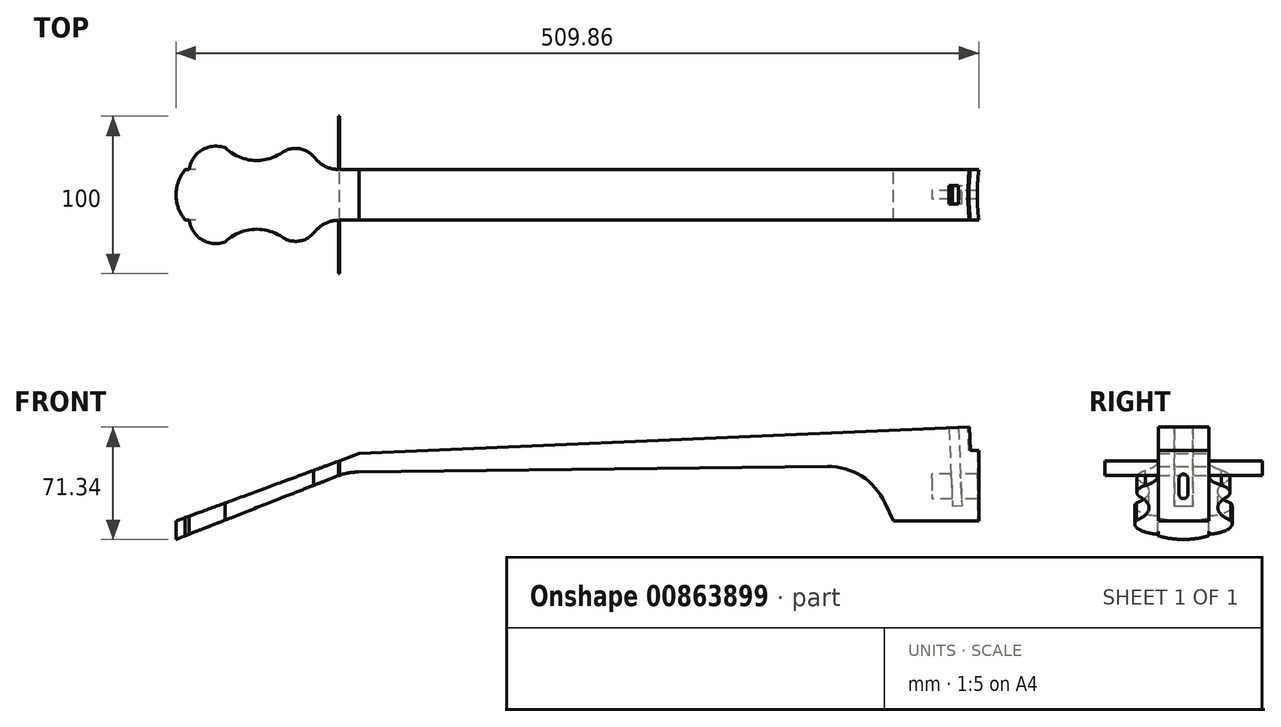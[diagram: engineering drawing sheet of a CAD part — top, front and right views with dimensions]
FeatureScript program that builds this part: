
annotation { "Feature Type Name" : "Feature", "Feature Type Description" : "" }
export const myFeature = defineFeature(function(context is Context, id is Id, definition is map)
    precondition{}
    {
        {
            var Q0;
            Q0=qCreatedBy(makeId("Front.planeOp"),FACE);
            var sketch = newSketch(context, id + "F0", { "sketchPlane" : qUnion([Q0])});
            skLineSegment(sketch, "E0.bottom", {"start": v(-76.22, 15.21) * mm, "end": v(250.9, 15.21) * mm});
            skLineSegment(sketch, "E0.top", {"start": v(195.63, -44.79) * mm, "end": v(250.9, -44.79) * mm});
            skLineSegment(sketch, "E0.right", {"start": v(250.9, 15.21) * mm, "end": v(250.9, -44.79) * mm});
            skPoint(sketch, "E1.orphan", {"position": v(250.9, 0) * mm});
            skLineSegment(sketch, "E2.bottom", {"start": v(250.9, 15.21) * mm, "end": v(-260.04, 15.21) * mm, "construction": true});
            skLineSegment(sketch, "E2.top", {"start": v(250.9, -44.79) * mm, "end": v(-260.04, -44.79) * mm, "construction": true});
            skLineSegment(sketch, "E2.left", {"start": v(250.9, 15.21) * mm, "end": v(250.9, -44.79) * mm, "construction": true});
            skLineSegment(sketch, "E2.right", {"start": v(-260.04, 15.21) * mm, "end": v(-260.04, -44.79) * mm, "construction": true});
            skLineSegment(sketch, "E3", {"start": v(250.9, 15.21) * mm, "end": v(-143.72, -2.02) * mm});
            skLineSegment(sketch, "E4", {"start": v(-143.72, -2.02) * mm, "end": v(-260.04, -44.79) * mm});
            skLineSegment(sketch, "E5", {"start": v(-158.15, -16.4) * mm, "end": v(-260.04, -56.44) * mm});
            skLineSegment(sketch, "E6", {"start": v(-144, -13.64) * mm, "end": v(153.56, -10.13) * mm});
            skLineSegment(sketch, "E7", {"start": v(195.63, -44.79) * mm, "end": v(190.35, -33.35) * mm});
            skPoint(sketch, "E8.visualSharp", {"position": v(-151.32, -13.72) * mm});
            skArc(sketch, "E8.filletArc", {"start": v(-144, -13.64) * mm, "mid": v(-151.2, -14.38) * mm, "end": v(-158.15, -16.4) * mm});
            skPoint(sketch, "E9.visualSharp", {"position": v(179.48, -9.82) * mm});
            skArc(sketch, "E9.filletArc", {"start": v(190.35, -33.35) * mm, "mid": v(175.39, -16.3) * mm, "end": v(153.56, -10.13) * mm});
            skPoint(sketch, "E10", {"position": v(-143.72, -2.02) * mm});
            skPoint(sketch, "E11", {"position": v(-260.04, -44.79) * mm});
            skLineSegment(sketch, "E12", {"start": v(-260.04, -44.79) * mm, "end": v(-260.04, -56.44) * mm});
            skPoint(sketch, "E13", {"position": v(-260.04, -56.44) * mm});
            skLineSegment(sketch, "E14", {"start": v(-143.72, -2.02) * mm, "end": v(-143.72, -13.63) * mm, "construction": true});
            skPoint(sketch, "E15", {"position": v(-143.72, -13.63) * mm});
            skSolve(sketch);
        }
        {
            var Q0;
            Q0=makeQuery(id+"F0.imprint","IMPRINT",FACE,{"disambiguationData":[TD([[makeQuery(id+"F0.imprint","IMPRINT",EDGE,{"derivedFrom":sQuery(id+"F0.wireOp",EDGE,"E0.bottom")}),-1.0]])]});
            var Q1;
            Q1=makeQuery(id+"F0.imprint","IMPRINT",FACE,{"disambiguationData":[TD([[makeQuery(id+"F0.imprint","IMPRINT",EDGE,{"derivedFrom":sQuery(id+"F0.wireOp",EDGE,"E0.top")}),1.0]])]});
            extrude(context, id + "F1", {"entities" : qUnion([Q0, Q1]), "endBound" : BoundingType.SYMMETRIC, "depth" : 32 * mm, "offsetDistance" : 25 * mm});
        }
        {
            var Q0;
            Q0=makeQuery(id+"F1.opExtrude","SWEPT_FACE",FACE,{"disambiguationData":[OSD([sQuery(id+"F0.wireOp",EDGE,"E0.top")])]});
            var sketch = newSketch(context, id + "F2", { "sketchPlane" : qUnion([Q0])});
            skLineSegment(sketch, "E16", {"start": v(240.9, 0) * mm, "end": v(568.8, 0) * mm, "construction": true});
            skPoint(sketch, "E17", {"position": v(388.9, 0) * mm});
            skCircle(sketch, "E18", {"center": v(388.9, 0) * mm, "radius": 140 * mm});
            skSolve(sketch);
        }
        {
            var Q0;
            Q0=sQuery(id+"F2.wireOp",VERTEX,"E17");
            var Q1;
            Q1=makeQuery(id+"F1.opExtrude","SWEPT_BODY",BODY,{"disambiguationData":[OSD([sQuery(id+"F0.wireOp",EDGE,"E0.top"),sQuery(id+"F0.wireOp",EDGE,"E0.right"),sQuery(id+"F0.wireOp",EDGE,"E3"),sQuery(id+"F0.wireOp",EDGE,"E4"),sQuery(id+"F0.wireOp",EDGE,"E5"),sQuery(id+"F0.wireOp",EDGE,"dch4oOjl-po2X-NTcd-wBgV-2fWfEdsUv7Ez"),sQuery(id+"F0.wireOp",EDGE,"E6"),sQuery(id+"F0.wireOp",EDGE,"E7"),sQuery(id+"F0.wireOp",EDGE,"E8.filletArc"),sQuery(id+"F0.wireOp",EDGE,"E9.filletArc")])]});
            hole(context, id + "F3", {"style" : HoleStyle.SIMPLE, "endStyle" : HoleEndStyle.THROUGH, "holeDiameter" : 280 * mm, "majorDiameter" : 5 * mm, "isTappedThrough" : true, "tappedDepth" : 12 * mm, "tapClearance" : 3, "locations" : qUnion([Q0]), "scope" : qUnion([Q1])});
        }
        {
            var Q0;
            Q0=qCreatedBy(makeId("Front.planeOp"),FACE);
            var sketch = newSketch(context, id + "F4", { "sketchPlane" : qUnion([Q0])});
            skLineSegment(sketch, "E19", {"start": v(-239.97, -48.56) * mm, "end": v(-260.04, -56.42) * mm});
            skLineSegment(sketch, "E20", {"start": v(-260.04, -44.79) * mm, "end": v(-156.2, -6.6) * mm});
            skLineSegment(sketch, "E21", {"start": v(-156.2, -6.6) * mm, "end": v(-156.2, -15.7) * mm, "construction": true});
            skLineSegment(sketch, "E22", {"start": v(-156.2, -6.6) * mm, "end": v(-156.2, -15.7) * mm});
            skPoint(sketch, "E23", {"position": v(-156.2, -15.7) * mm});
            skLineSegment(sketch, "E24", {"start": v(-260.04, -44.79) * mm, "end": v(-260.04, -56.44) * mm});
            skLineSegment(sketch, "E25", {"start": v(-260.04, -56.44) * mm, "end": v(-156.2, -15.7) * mm});
            skSolve(sketch);
        }
        {
            var Q0;
            Q0=makeQuery(id+"F4.imprint","IMPRINT",FACE,{"disambiguationData":[TD([[makeQuery(id+"F4.imprint","IMPRINT",EDGE,{"derivedFrom":sQuery(id+"F4.wireOp",EDGE,"E19")}),-1.0]])]});
            extrude(context, id + "F5", {"entities" : qUnion([Q0]), "operationType" : NewBodyOperationType.ADD, "endBound" : BoundingType.SYMMETRIC, "depth" : 100 * mm, "offsetDistance" : 25 * mm});
        }
        {
            var Q0;
            Q0=qCreatedBy(makeId("Top.planeOp"),FACE);
            var sketch = newSketch(context, id + "F6", { "sketchPlane" : qUnion([Q0])});
            skLineSegment(sketch, "E26", {"start": v(-22.9, 0) * mm, "end": v(-271.53, 0) * mm, "construction": true});
            skPoint(sketch, "E27", {"position": v(-156.8, 0) * mm});
            skPoint(sketch, "E28", {"position": v(-260.04, 0) * mm});
            skPoint(sketch, "E29", {"position": v(-260.04, 50) * mm});
            skPoint(sketch, "E30", {"position": v(-156.8, 50) * mm});
            skArc(sketch, "E31", {"start": v(-172.53, 24.22) * mm, "mid": v(-165.64, 18.27) * mm, "end": v(-156.8, 16.12) * mm});
            skArc(sketch, "E32", {"start": v(-254.15, 16.1) * mm, "mid": v(-258.52, 8.57) * mm, "end": v(-260.04, 0) * mm});
            skLineSegment(sketch, "E33", {"start": v(-254.15, 16.1) * mm, "end": v(-251.7, 16.1) * mm});
            skArc(sketch, "E34", {"start": v(-228.96, 29.97) * mm, "mid": v(-243.62, 28.43) * mm, "end": v(-251.7, 16.1) * mm});
            skArc(sketch, "E35", {"start": v(-228.96, 29.97) * mm, "mid": v(-211.3, 21.9) * mm, "end": v(-192.54, 26.9) * mm});
            skArc(sketch, "E36", {"start": v(-192.54, 26.9) * mm, "mid": v(-181.35, 29.3) * mm, "end": v(-171.7, 23.13) * mm});
            skLineSegment(sketch, "E37", {"start": v(-260.04, 50) * mm, "end": v(-260.04, 0) * mm});
            skLineSegment(sketch, "E38", {"start": v(-260.04, 50) * mm, "end": v(-156.8, 50) * mm});
            skLineSegment(sketch, "E39", {"start": v(-156.8, 16.12) * mm, "end": v(-156.8, 50) * mm});
            skArc(sketch, "E40.MirrorCS", {"start": v(-228.96, -29.97) * mm, "mid": v(-243.62, -28.43) * mm, "end": v(-251.7, -16.1) * mm});
            skLineSegment(sketch, "E41.MirrorCS", {"start": v(-254.15, -16.1) * mm, "end": v(-251.7, -16.1) * mm});
            skArc(sketch, "E42.MirrorCS", {"start": v(-254.15, -16.1) * mm, "mid": v(-258.52, -8.57) * mm, "end": v(-260.04, 0) * mm});
            skLineSegment(sketch, "E43.MirrorCS", {"start": v(-260.04, -50) * mm, "end": v(-260.04, 0) * mm});
            skArc(sketch, "E44.MirrorCS", {"start": v(-228.96, -29.97) * mm, "mid": v(-211.3, -21.9) * mm, "end": v(-192.54, -26.9) * mm});
            skLineSegment(sketch, "E45.MirrorCS", {"start": v(-260.04, -50) * mm, "end": v(-156.8, -50) * mm});
            skArc(sketch, "E46.MirrorCS", {"start": v(-192.54, -26.9) * mm, "mid": v(-181.35, -29.3) * mm, "end": v(-171.7, -23.13) * mm});
            skArc(sketch, "E47.MirrorCS", {"start": v(-172.53, -24.22) * mm, "mid": v(-165.64, -18.27) * mm, "end": v(-156.8, -16.12) * mm});
            skLineSegment(sketch, "E48.MirrorCS", {"start": v(-156.8, -16.12) * mm, "end": v(-156.8, -50) * mm});
            skSolve(sketch);
        }
        {
            var Q0;
            Q0 = qSketchRegion(id + "F6", true);
            extrude(context, id + "F7", {"entities" : qUnion([Q0]), "operationType" : NewBodyOperationType.REMOVE, "oppositeDirection" : true, "depth" : 100 * mm, "offsetDistance" : 25 * mm});
        }
        {
            var Q0;
            Q0=makeQuery(id+"F1.opExtrude","SWEPT_FACE",FACE,{"disambiguationData":[OSD([sQuery(id+"F0.wireOp",EDGE,"E3")])]});
            var sketch = newSketch(context, id + "F8", { "sketchPlane" : qUnion([Q0])});
            skPoint(sketch, "E49.startSnap0", {"position": v(249.32, 0) * mm});
            skLineSegment(sketch, "E50", {"start": v(246.75, 0) * mm, "end": v(167.53, 0) * mm, "construction": true});
            skLineSegment(sketch, "E51", {"start": v(237.36, 5.84) * mm, "end": v(237.36, 0) * mm});
            skLineSegment(sketch, "E52", {"start": v(237.36, 5.84) * mm, "end": v(231.35, 5.84) * mm});
            skLineSegment(sketch, "E53", {"start": v(231.35, 5.84) * mm, "end": v(231.35, 0) * mm});
            skPoint(sketch, "E54.MirrorCS.end.orphan", {"position": v(237.36, 0) * mm});
            skLineSegment(sketch, "E55.MirrorCS", {"start": v(237.36, -5.84) * mm, "end": v(237.36, 0) * mm});
            skLineSegment(sketch, "E56.MirrorCS", {"start": v(237.36, -5.84) * mm, "end": v(231.35, -5.84) * mm});
            skLineSegment(sketch, "E57.MirrorCS", {"start": v(231.35, -5.84) * mm, "end": v(231.35, 0) * mm});
            skSolve(sketch);
        }
        {
            var Q0;
            Q0 = qSketchRegion(id + "F8", true);
            extrude(context, id + "F9", {"entities" : qUnion([Q0]), "operationType" : NewBodyOperationType.REMOVE, "oppositeDirection" : true, "depth" : 50 * mm, "offsetDistance" : 25 * mm, "hasDraft" : true, "draftAngle" : 0 * degree, "draftPullDirection" : true});
        }
        {
            var Q0;
            Q0=qCreatedBy(makeId("Right.planeOp"),FACE);
            var sketch = newSketch(context, id + "F10", { "sketchPlane" : qUnion([Q0])});
            skLineSegment(sketch, "E58", {"start": v(-41.25, 0) * mm, "end": v(48.15, 0) * mm, "construction": true});
            skLineSegment(sketch, "E59", {"start": v(0, 14.2) * mm, "end": v(0, -27.81) * mm, "construction": true});
            skLineSegment(sketch, "E60.right", {"start": v(0, -17.75) * mm, "end": v(0, -27.81) * mm});
            skArc(sketch, "E61", {"start": v(-2.78, -17.75) * mm, "mid": v(-1.97, -15.78) * mm, "end": v(0, -14.97) * mm});
            skArc(sketch, "E62", {"start": v(-2.78, -27.81) * mm, "mid": v(-1.97, -29.78) * mm, "end": v(0, -30.6) * mm});
            skLineSegment(sketch, "E63", {"start": v(-2.78, -17.75) * mm, "end": v(-2.78, -27.81) * mm});
            skArc(sketch, "E64.MirrorCS", {"start": v(2.78, -17.75) * mm, "mid": v(1.97, -15.78) * mm, "end": v(0, -14.97) * mm});
            skLineSegment(sketch, "E65.MirrorCS", {"start": v(2.78, -17.75) * mm, "end": v(2.78, -27.81) * mm});
            skArc(sketch, "E66.MirrorCS", {"start": v(2.78, -27.81) * mm, "mid": v(1.97, -29.78) * mm, "end": v(0, -30.6) * mm});
            skSolve(sketch);
        }
        {
            var Q0;
            Q0 = qSketchRegion(id + "F10", true);
            extrude(context, id + "F11", {"entities" : qUnion([Q0]), "operationType" : NewBodyOperationType.REMOVE, "endBound" : BoundingType.THROUGH_ALL, "depth" : 25 * mm, "offsetDistance" : 25 * mm, "hasSecondDirection" : true, "secondDirectionOppositeDirection" : false, "secondDirectionDepth" : 220 * mm});
        }
        {
            var Q0;
            Q0=makeQuery(id+"F1.opExtrude","SWEPT_FACE",FACE,{"disambiguationData":[OSD([sQuery(id+"F0.wireOp",EDGE,"E3")])]});
            var sketch = newSketch(context, id + "F12", { "sketchPlane" : qUnion([Q0])});
            skLineSegment(sketch, "E67", {"start": v(-143.68, 0) * mm, "end": v(485.18, 0) * mm, "construction": true});
            skPoint(sketch, "E68", {"position": v(389.32, 0) * mm});
            skCircle(sketch, "E69", {"center": v(389.32, 0) * mm, "radius": 146 * mm});
            skCircle(sketch, "E70", {"center": v(382.3, 0) * mm, "radius": 5.84 * mm});
            skSolve(sketch);
        }
        {
            var Q0;
            Q0 = qSketchRegion(id + "F12", true);
            extrude(context, id + "F13", {"entities" : qUnion([Q0]), "operationType" : NewBodyOperationType.REMOVE, "oppositeDirection" : true, "depth" : 15 * mm, "offsetDistance" : 25 * mm});
        }
    });
